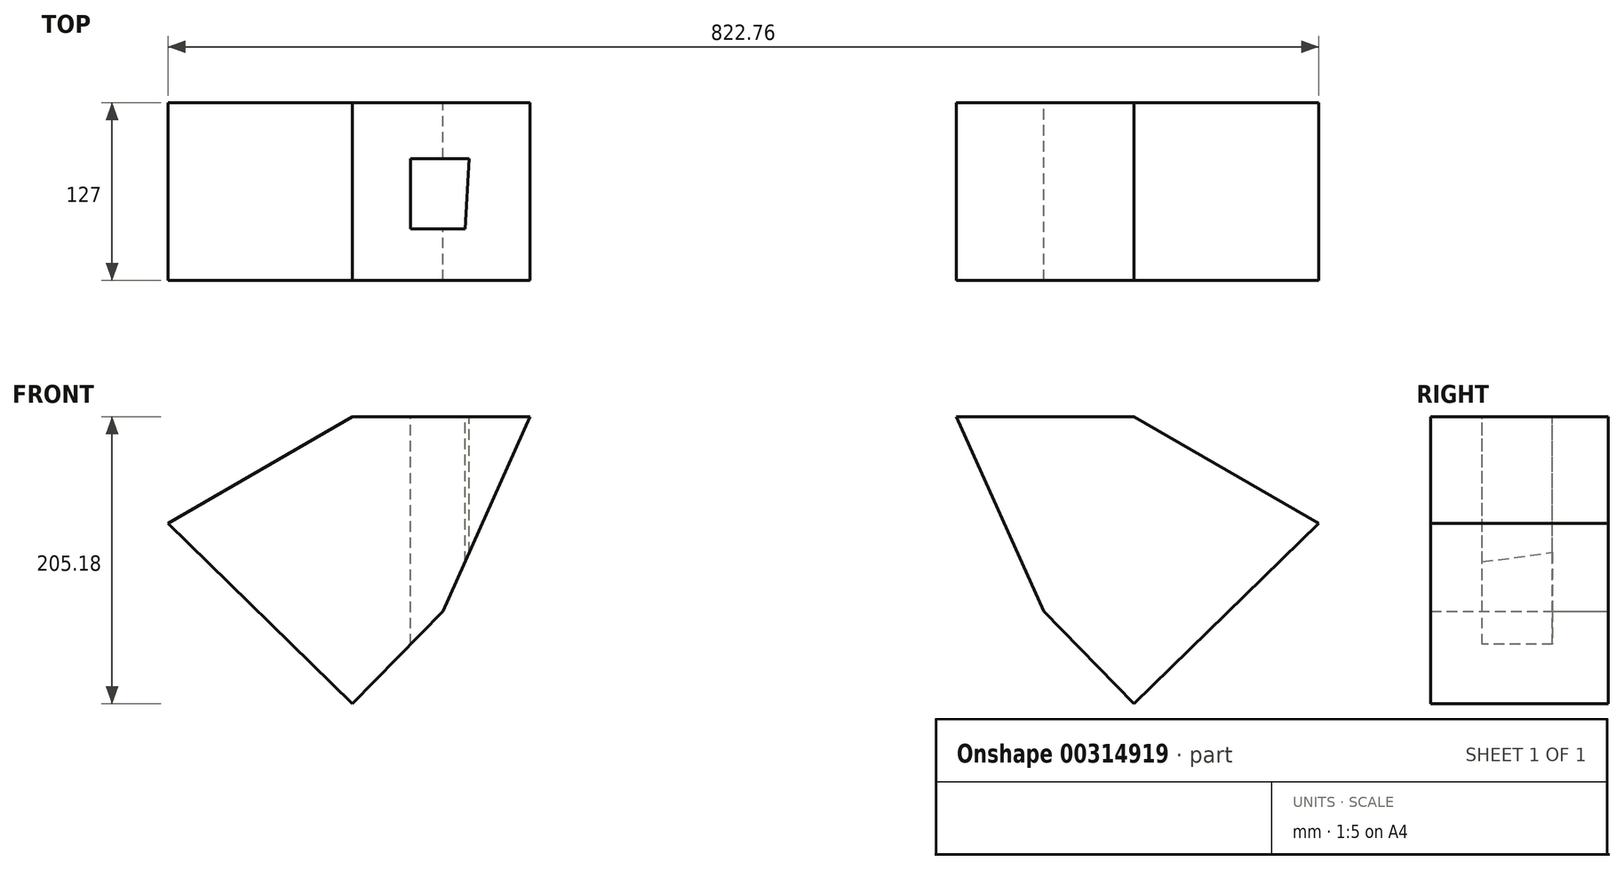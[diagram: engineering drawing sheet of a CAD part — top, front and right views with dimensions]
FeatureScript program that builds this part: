
annotation { "Feature Type Name" : "Feature", "Feature Type Description" : "" }
export const myFeature = defineFeature(function(context is Context, id is Id, definition is map)
    precondition{}
    {
        {
            var Q0;
            Q0=qCreatedBy(makeId("Front.planeOp"),FACE);
            var sketch = newSketch(context, id + "F0", { "sketchPlane" : qUnion([Q0])});
            skLineSegment(sketch, "E0", {"start": v(-152.4, 139.05) * mm, "end": v(-279.4, 139.05) * mm});
            skLineSegment(sketch, "E1", {"start": v(-279.4, 139.05) * mm, "end": v(-411.38, 62.85) * mm});
            skLineSegment(sketch, "E2", {"start": v(-411.38, 62.85) * mm, "end": v(-279.4, -66.13) * mm});
            skLineSegment(sketch, "E3", {"start": v(-279.4, -66.13) * mm, "end": v(-214.78, 0) * mm});
            skLineSegment(sketch, "E4", {"start": v(-214.78, 0) * mm, "end": v(-152.4, 139.05) * mm});
            skSolve(sketch);
        }
        {
            var Q0;
            Q0=makeQuery(id+"F0.imprint","IMPRINT",FACE,{"disambiguationData":[TD([[makeQuery(id+"F0.imprint","IMPRINT",EDGE,{"derivedFrom":sQuery(id+"F0.wireOp",EDGE,"E0")}),1.0]])]});
            extrude(context, id + "F1", {"entities" : qUnion([Q0]), "depth" : 127 * mm});
        }
        {
            var Q0;
            Q0=makeQuery(id+"F1.opExtrude","SWEPT_FACE",FACE,{"disambiguationData":[OSD([sQuery(id+"F0.wireOp",EDGE,"E0")])]});
            var sketch = newSketch(context, id + "F2", { "sketchPlane" : qUnion([Q0])});
            skLineSegment(sketch, "E5", {"start": v(-195.91, -39.93) * mm, "end": v(-237.91, -39.93) * mm});
            skLineSegment(sketch, "E6", {"start": v(-237.91, -39.93) * mm, "end": v(-237.91, -90.08) * mm});
            skLineSegment(sketch, "E7", {"start": v(-237.91, -90.08) * mm, "end": v(-198.9, -90.08) * mm});
            skLineSegment(sketch, "E8", {"start": v(-198.9, -90.08) * mm, "end": v(-195.91, -39.93) * mm});
            skSolve(sketch);
        }
        {
            var Q0;
            Q0=makeQuery(id+"F1.opExtrude","SWEPT_BODY",BODY,{"disambiguationData":[OSD([sQuery(id+"F0.wireOp",EDGE,"E0"),sQuery(id+"F0.wireOp",EDGE,"E1"),sQuery(id+"F0.wireOp",EDGE,"E2"),sQuery(id+"F0.wireOp",EDGE,"E3"),sQuery(id+"F0.wireOp",EDGE,"E4")])]});
            var Q1;
            Q1=qCreatedBy(makeId("Right.planeOp"),FACE);
            mirror(context, id + "F3", {"entities" : qUnion([Q0]), "mirrorPlane" : qUnion([Q1])});
        }
        {
            var Q0;
            Q0=makeQuery(id+"F2.imprint","IMPRINT",FACE,{"disambiguationData":[TD([[makeQuery(id+"F2.imprint","IMPRINT",EDGE,{"derivedFrom":sQuery(id+"F2.wireOp",EDGE,"E5")}),1.0]])]});
            extrude(context, id + "F4", {"entities" : qUnion([Q0]), "operationType" : NewBodyOperationType.REMOVE, "endBound" : BoundingType.THROUGH_ALL, "oppositeDirection" : true, "depth" : 381 * mm});
        }
    });
